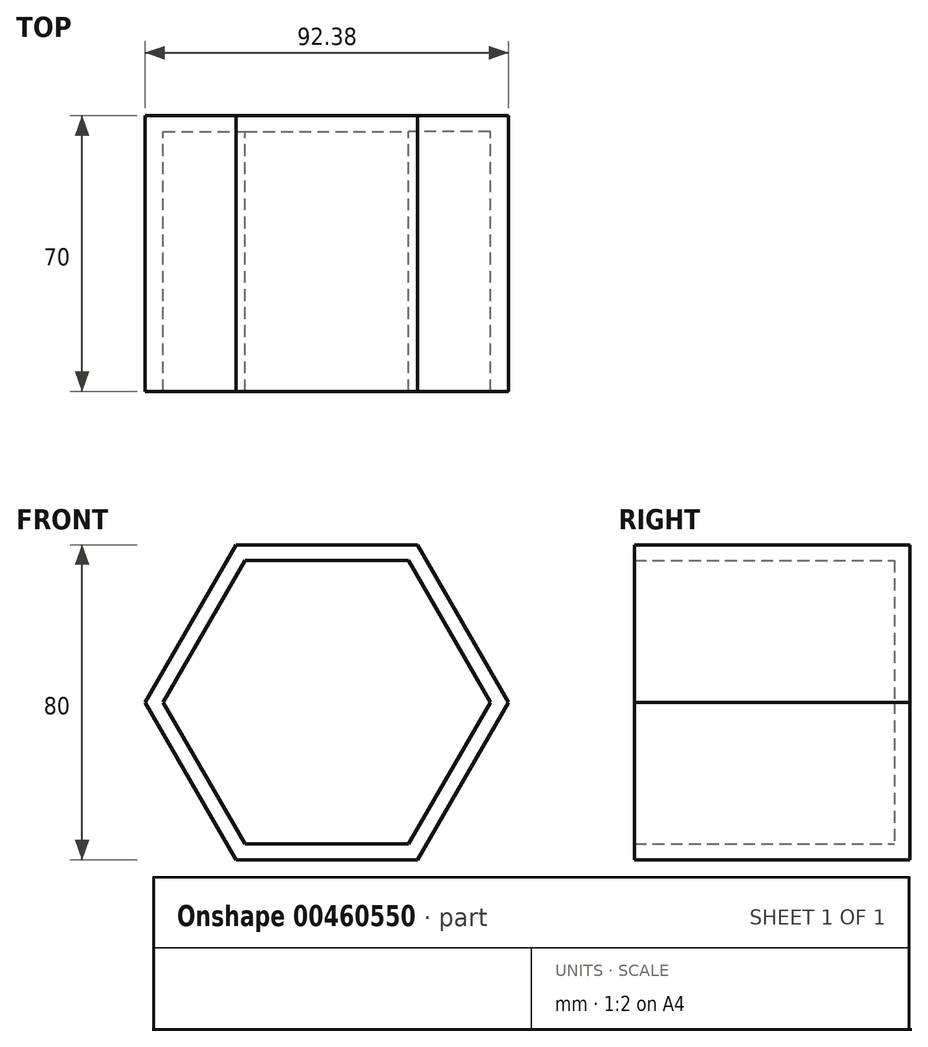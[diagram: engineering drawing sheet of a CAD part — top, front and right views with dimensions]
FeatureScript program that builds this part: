
annotation { "Feature Type Name" : "Feature", "Feature Type Description" : "" }
export const myFeature = defineFeature(function(context is Context, id is Id, definition is map)
    precondition{}
    {
        {
            var Q0;
            Q0=qCreatedBy(makeId("Front.planeOp"),FACE);
            var sketch = newSketch(context, id + "F0", { "sketchPlane" : qUnion([Q0])});
            skCircle(sketch, "E0.cCircle", {"center": v(0, 0) * mm, "radius": 40 * mm, "construction": true});
            skLineSegment(sketch, "E0.0", {"start": v(46.19, 0) * mm, "end": v(23.1, -40) * mm});
            skLineSegment(sketch, "E0.1", {"start": v(23.1, -40) * mm, "end": v(-23.1, -40) * mm});
            skLineSegment(sketch, "E0.2", {"start": v(-23.1, -40) * mm, "end": v(-46.19, 0) * mm});
            skLineSegment(sketch, "E0.3", {"start": v(-46.19, 0) * mm, "end": v(-23.1, 40) * mm});
            skLineSegment(sketch, "E0.4", {"start": v(-23.1, 40) * mm, "end": v(23.1, 40) * mm});
            skLineSegment(sketch, "E0.5", {"start": v(23.1, 40) * mm, "end": v(46.19, 0) * mm});
            skPoint(sketch, "E0.0.midPoint", {"position": v(34.64, -20) * mm});
            skSolve(sketch);
        }
        {
            var Q0;
            Q0=makeQuery(id+"F0.imprint","IMPRINT",FACE,{"disambiguationData":[TD([[makeQuery(id+"F0.imprint","IMPRINT",EDGE,{"derivedFrom":sQuery(id+"F0.wireOp",EDGE,"E0.0")}),-1.0]])]});
            extrude(context, id + "F1", {"entities" : qUnion([Q0]), "depth" : 70 * mm});
        }
        {
            var Q0;
            Q0=makeQuery(id+"F1.opExtrude","CAP_FACE",FACE,{"disambiguationData":[OSD([sQuery(id+"F0.wireOp",EDGE,"E0.0"),sQuery(id+"F0.wireOp",EDGE,"E0.1"),sQuery(id+"F0.wireOp",EDGE,"E0.2"),sQuery(id+"F0.wireOp",EDGE,"E0.3"),sQuery(id+"F0.wireOp",EDGE,"E0.4"),sQuery(id+"F0.wireOp",EDGE,"E0.5")])],"isStart":false});
            shell(context, id + "F2", {"entities" : qUnion([Q0]), "thickness" : 4 * mm});
        }
    });
